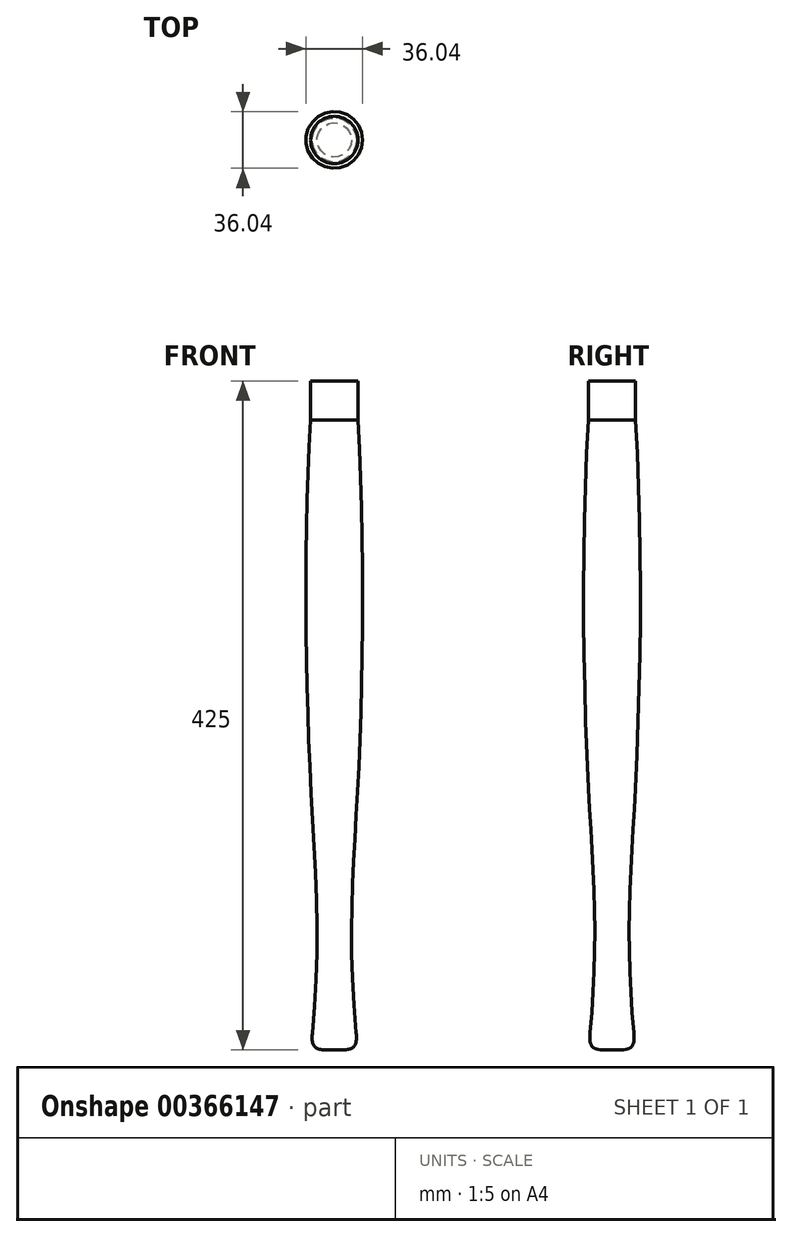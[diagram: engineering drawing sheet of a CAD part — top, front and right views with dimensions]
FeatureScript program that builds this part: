
annotation { "Feature Type Name" : "Feature", "Feature Type Description" : "" }
export const myFeature = defineFeature(function(context is Context, id is Id, definition is map)
    precondition{}
    {
        {
            var Q0;
            Q0=qCreatedBy(makeId("Front.planeOp"),FACE);
            var sketch = newSketch(context, id + "F0", { "sketchPlane" : qUnion([Q0])});
            skLineSegment(sketch, "E0", {"start": v(0, 0) * mm, "end": v(-15, 0) * mm});
            skLineSegment(sketch, "E1", {"start": v(-15, 0) * mm, "end": v(-15, -25) * mm});
            skLineSegment(sketch, "E2", {"start": v(-15, -25) * mm, "end": v(-15, -425) * mm, "construction": true});
            skFitSpline(sketch, "E3", {"points": [v(-15, -25) * mm, v(-15, -256.4) * mm, v(-15, -425) * mm], "startDerivative": vector(-25.54, -424.43) * mm, "endDerivative": vector(-48.86, -450.94) * mm});
            skLineSegment(sketch, "E4", {"start": v(-15, -425) * mm, "end": v(0, -425) * mm});
            skLineSegment(sketch, "E5", {"start": v(0, 0) * mm, "end": v(0, -425) * mm});
            skPoint(sketch, "E6", {"position": v(-7.5, -425) * mm});
            skSolve(sketch);
        }
        {
            var Q0;
            Q0=makeQuery(id+"F0.imprint","IMPRINT",FACE,{"disambiguationData":[TD([[makeQuery(id+"F0.imprint","IMPRINT",EDGE,{"derivedFrom":sQuery(id+"F0.wireOp",EDGE,"E0")}),1.0]])]});
            var Q1;
            Q1=sQuery(id+"F0.wireOp",EDGE,"E5");
            revolve(context, id + "F1", {"entities" : qUnion([Q0]), "axis" : qUnion([Q1]), "revolveType" : RevolveType.FULL});
        }
        {
            var Q0;
            Q0=makeQuery(id+"F1.opRevolve","SWEPT_EDGE",EDGE,{"disambiguationData":[OSD([sQuery(id+"F0.wireOp",EDGE,"E3"),sQuery(id+"F0.wireOp",EDGE,"E4")])]});
            fillet(context, id + "F2", {"entities" : qUnion([Q0]), "radius" : 10 * mm, "tangentPropagation" : true, "rho" : 0.6, "crossSection" : FilletCrossSection.CONIC, "allowEdgeOverflow" : false});
        }
    });
